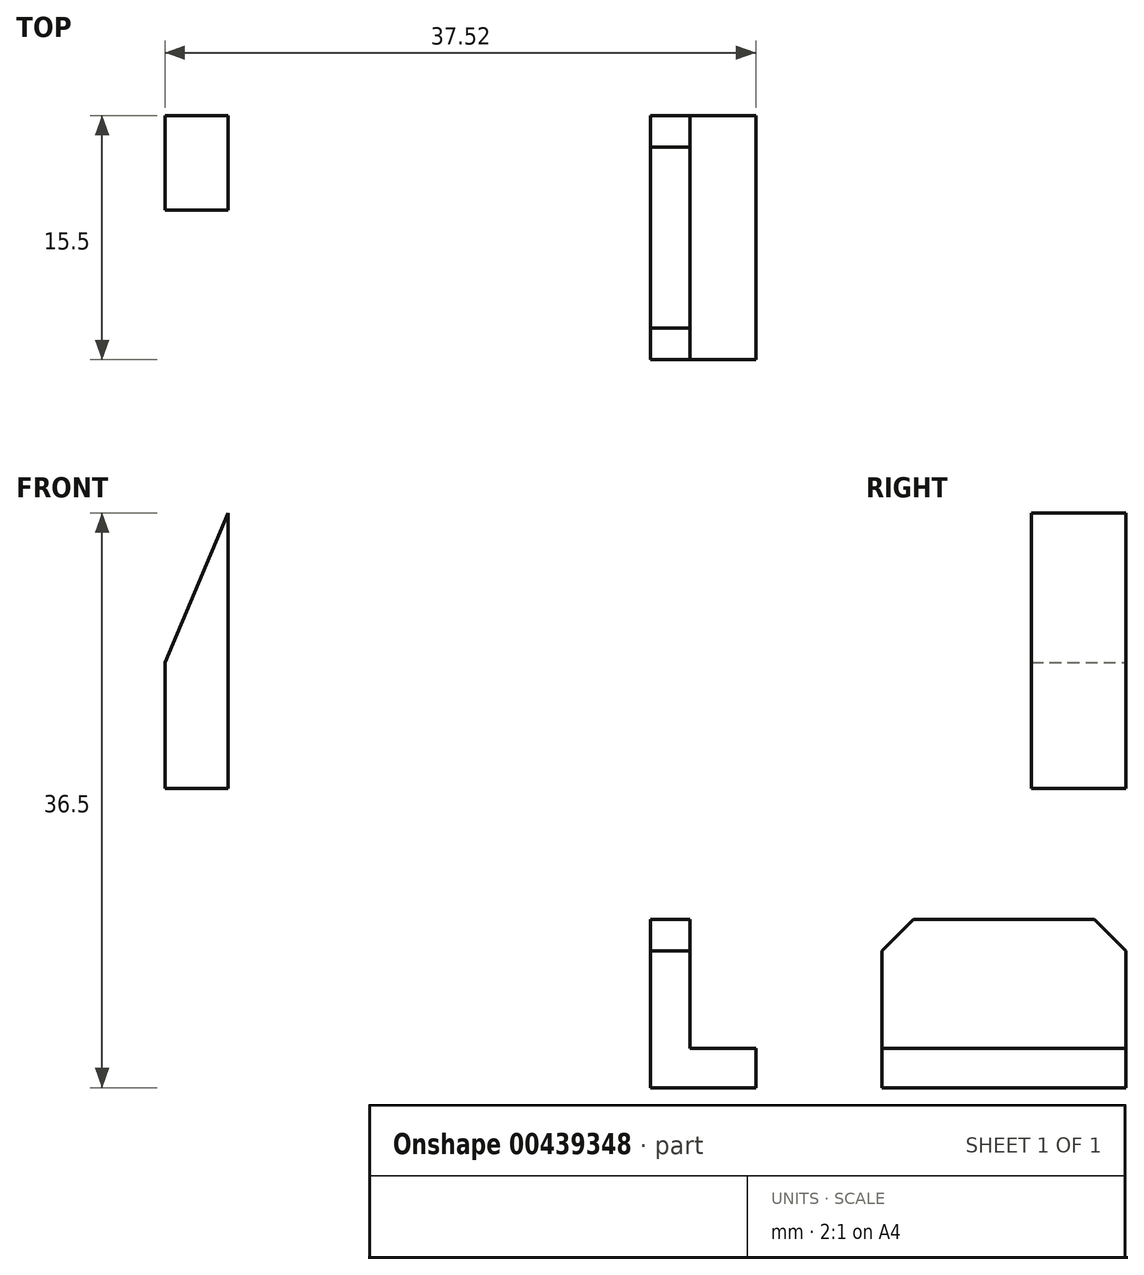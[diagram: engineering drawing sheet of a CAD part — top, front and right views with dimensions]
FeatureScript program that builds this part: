
annotation { "Feature Type Name" : "Feature", "Feature Type Description" : "" }
export const myFeature = defineFeature(function(context is Context, id is Id, definition is map)
    precondition{}
    {
        {
            var Q0;
            Q0=qCreatedBy(makeId("Front.planeOp"),FACE);
            var sketch = newSketch(context, id + "F0", { "sketchPlane" : qUnion([Q0])});
            skLineSegment(sketch, "E0", {"start": v(-2.5, -8.3) * mm, "end": v(0, -8.3) * mm});
            skLineSegment(sketch, "E1", {"start": v(-2.5, -8.3) * mm, "end": v(-2.5, -19) * mm});
            skLineSegment(sketch, "E2", {"start": v(-2.5, -19) * mm, "end": v(4.2, -19) * mm});
            skLineSegment(sketch, "E3", {"start": v(4.2, -19) * mm, "end": v(4.2, -16.5) * mm});
            skLineSegment(sketch, "E4", {"start": v(4.2, -16.5) * mm, "end": v(0, -16.5) * mm});
            skLineSegment(sketch, "E5", {"start": v(0, -16.5) * mm, "end": v(0, -8.3) * mm});
            skSolve(sketch);
        }
        {
            var Q0;
            Q0=makeQuery(id+"F0.imprint","IMPRINT",FACE,{"disambiguationData":[TD([[makeQuery(id+"F0.imprint","IMPRINT",EDGE,{"derivedFrom":sQuery(id+"F0.wireOp",EDGE,"E0")}),-1.0]])]});
            extrude(context, id + "F1", {"entities" : qUnion([Q0]), "depth" : 15.5 * mm});
        }
        {
            var Q0;
            Q0=makeQuery(id+"F1.opExtrude","CAP_EDGE",EDGE,{"disambiguationData":[OSD([sQuery(id+"F0.wireOp",EDGE,"E0")])],"isStart":false});
            chamfer(context, id + "F2", {"entities" : qUnion([Q0]), "width" : 2 * mm, "tangentPropagation" : true});
        }
        {
            var Q0;
            Q0=makeQuery(id+"F1.opExtrude","CAP_EDGE",EDGE,{"disambiguationData":[OSD([sQuery(id+"F0.wireOp",EDGE,"E0")])],"isStart":true});
            chamfer(context, id + "F3", {"entities" : qUnion([Q0]), "width" : 2 * mm, "tangentPropagation" : true});
        }
        {
            var Q0;
            Q0=qCreatedBy(makeId("Front.planeOp"),FACE);
            var sketch = newSketch(context, id + "F4", { "sketchPlane" : qUnion([Q0])});
            skLineSegment(sketch, "E6", {"start": v(-29.32, 0) * mm, "end": v(-33.32, 0) * mm});
            skLineSegment(sketch, "E7", {"start": v(-33.32, 0) * mm, "end": v(-33.32, 8) * mm});
            skLineSegment(sketch, "E8", {"start": v(-33.32, 8) * mm, "end": v(-29.32, 17.5) * mm});
            skLineSegment(sketch, "E9", {"start": v(-29.32, 0) * mm, "end": v(-29.32, 17.5) * mm});
            skSolve(sketch);
        }
        {
            var Q0;
            Q0=makeQuery(id+"F4.imprint","IMPRINT",FACE,{"disambiguationData":[TD([[makeQuery(id+"F4.imprint","IMPRINT",EDGE,{"derivedFrom":sQuery(id+"F4.wireOp",EDGE,"E6")}),-1.0]])]});
            extrude(context, id + "F5", {"entities" : qUnion([Q0]), "depth" : 6 * mm});
        }
    });
